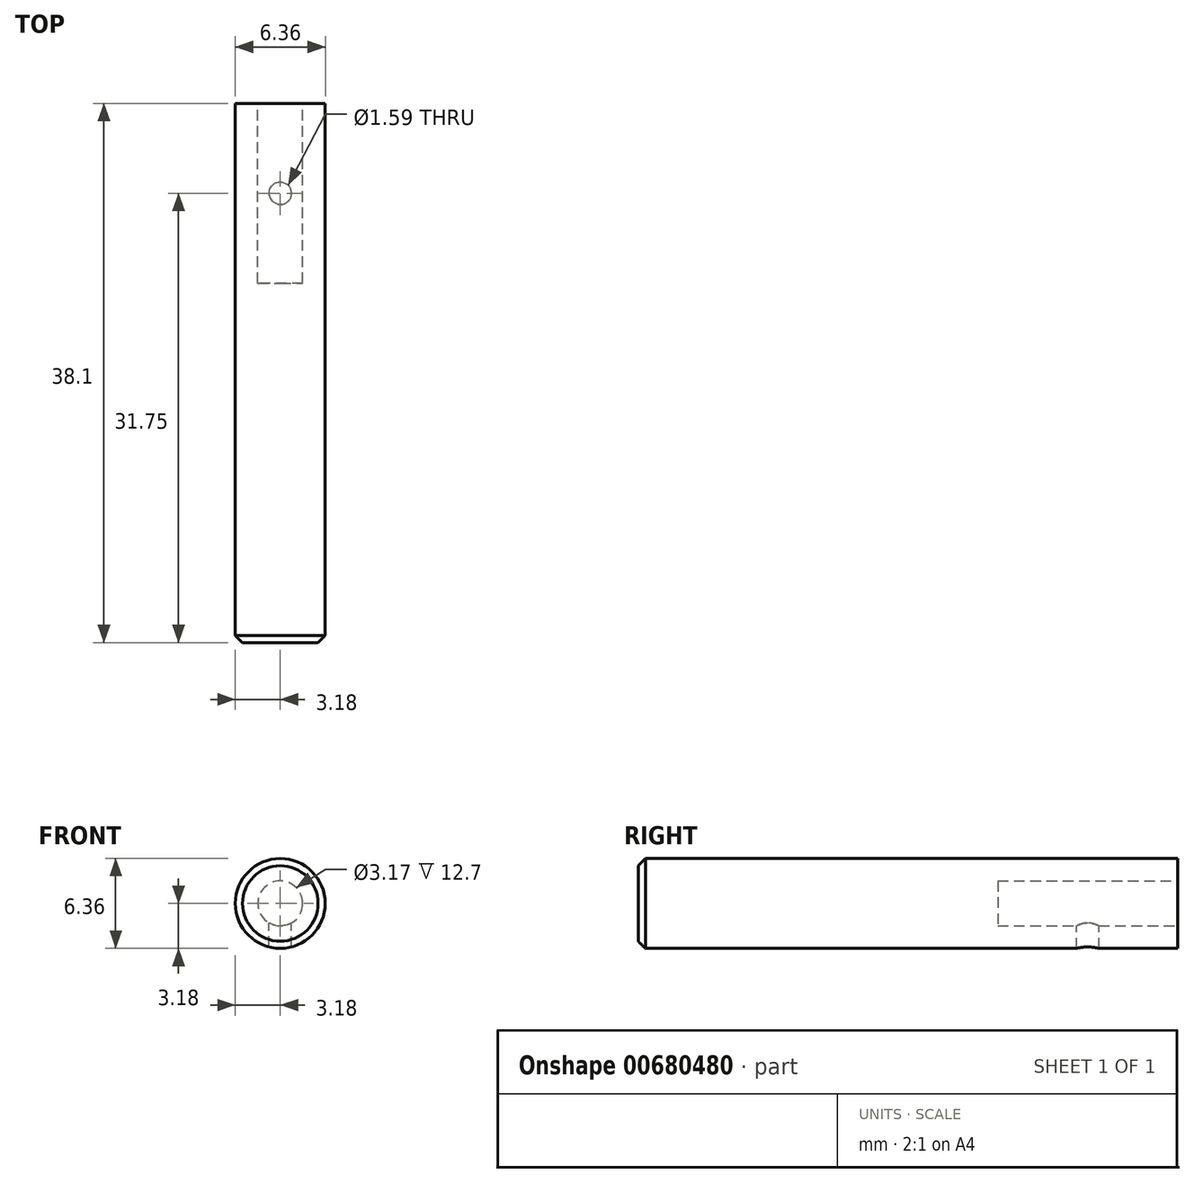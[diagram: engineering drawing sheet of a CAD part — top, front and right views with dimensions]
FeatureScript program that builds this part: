
annotation { "Feature Type Name" : "Feature", "Feature Type Description" : "" }
export const myFeature = defineFeature(function(context is Context, id is Id, definition is map)
    precondition{}
    {
        {
            var Q0;
            Q0=qCreatedBy(makeId("Front.planeOp"),FACE);
            var sketch = newSketch(context, id + "F0", { "sketchPlane" : qUnion([Q0])});
            skCircle(sketch, "E0", {"center": v(0, 0) * mm, "radius": 3.18 * mm});
            skSolve(sketch);
        }
        {
            var Q0;
            Q0=makeQuery(id+"F0.imprint","IMPRINT",FACE,{"disambiguationData":[TD([[makeQuery(id+"F0.imprint","IMPRINT",EDGE,{"derivedFrom":sQuery(id+"F0.wireOp",EDGE,"E0")}),1.0]])]});
            extrude(context, id + "F1", {"entities" : qUnion([Q0]), "depth" : 38.1 * mm, "offsetDistance" : 25.4 * mm});
        }
        {
            var Q0;
            Q0=makeQuery(id+"F1.opExtrude","CAP_FACE",FACE,{"disambiguationData":[OSD([sQuery(id+"F0.wireOp",EDGE,"E0")])],"isStart":true});
            var sketch = newSketch(context, id + "F2", { "sketchPlane" : qUnion([Q0])});
            skCircle(sketch, "E1", {"center": v(0, 0) * mm, "radius": 1.59 * mm});
            skSolve(sketch);
        }
        {
            var Q0;
            Q0=makeQuery(id+"F2.imprint","IMPRINT",FACE,{"disambiguationData":[TD([[makeQuery(id+"F2.imprint","IMPRINT",EDGE,{"derivedFrom":sQuery(id+"F2.wireOp",EDGE,"E1")}),1.0]])]});
            extrude(context, id + "F3", {"entities" : qUnion([Q0]), "operationType" : NewBodyOperationType.REMOVE, "oppositeDirection" : true, "depth" : 12.7 * mm, "offsetDistance" : 25.4 * mm});
        }
        {
            var Q0;
            Q0=qCreatedBy(makeId("Top.planeOp"),FACE);
            var sketch = newSketch(context, id + "F4", { "sketchPlane" : qUnion([Q0])});
            skCircle(sketch, "E2", {"center": v(0, -6.35) * mm, "radius": 0.8 * mm});
            skSolve(sketch);
        }
        {
            var Q0;
            Q0=makeQuery(id+"F4.imprint","IMPRINT",FACE,{"disambiguationData":[TD([[makeQuery(id+"F4.imprint","IMPRINT",EDGE,{"derivedFrom":sQuery(id+"F4.wireOp",EDGE,"E2")}),1.0]])]});
            extrude(context, id + "F5", {"entities" : qUnion([Q0]), "operationType" : NewBodyOperationType.REMOVE, "endBound" : BoundingType.THROUGH_ALL, "oppositeDirection" : true, "depth" : 25.4 * mm, "offsetDistance" : 25.4 * mm});
        }
        {
            var Q0;
            Q0=makeQuery(id+"F1.opExtrude","CAP_EDGE",EDGE,{"disambiguationData":[OSD([sQuery(id+"F0.wireOp",EDGE,"E0")])],"isStart":false});
            chamfer(context, id + "F6", {"entities" : qUnion([Q0]), "width" : 0.5 * mm, "tangentPropagation" : true});
        }
    });
